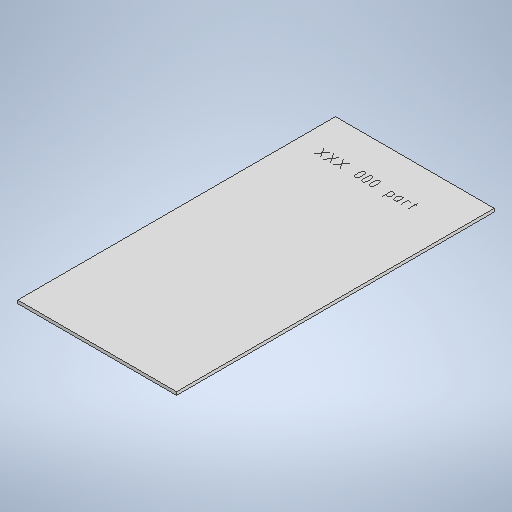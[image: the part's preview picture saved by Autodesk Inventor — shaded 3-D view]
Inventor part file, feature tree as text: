
AUTODESK INVENTOR PART (.ipt)
format: ipt  version: 2025 (Build 290162010, 162A)  size: 248,320 bytes
history: native  units: mm
features: other x2, sketch x2, sheet_metal_op x1
ambient origin geometry x8: Origin, YZ Plane, XZ Plane, XY Plane, X Axis, Y Axis, Z Axis, Center Point
bodies: Solid1 (feature_tree)
feature tree (5):
  sheet_metal_op  "Face1"
  other  "Mark2"
  sketch  "Sketch1"  dims[d0=100.0mm]
  other  "Plate1"
  sketch  "Sketch3"  dims[d1=200.0mm d2=2.0mm]
